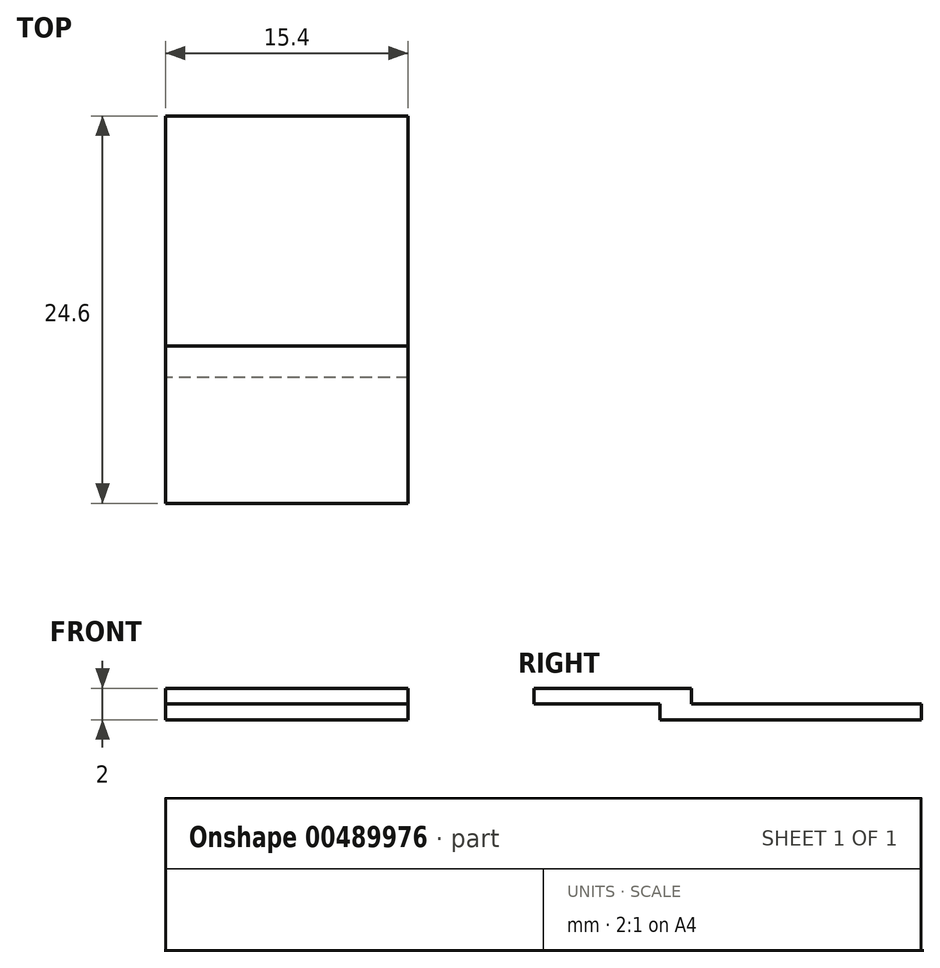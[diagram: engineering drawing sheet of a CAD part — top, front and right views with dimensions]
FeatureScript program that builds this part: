
annotation { "Feature Type Name" : "Feature", "Feature Type Description" : "" }
export const myFeature = defineFeature(function(context is Context, id is Id, definition is map)
    precondition{}
    {
        {
            var Q0;
            Q0=qCreatedBy(makeId("Top.planeOp"),FACE);
            var sketch = newSketch(context, id + "F0", { "sketchPlane" : qUnion([Q0])});
            skLineSegment(sketch, "E0.bottom", {"start": v(7.7, -8.3) * mm, "end": v(-7.7, -8.3) * mm});
            skLineSegment(sketch, "E0.top", {"start": v(7.7, 8.3) * mm, "end": v(-7.7, 8.3) * mm});
            skLineSegment(sketch, "E0.left", {"start": v(7.7, -8.3) * mm, "end": v(7.7, 8.3) * mm});
            skLineSegment(sketch, "E0.right", {"start": v(-7.7, -8.3) * mm, "end": v(-7.7, 8.3) * mm});
            skPoint(sketch, "E0.middle", {"position": v(0, 0) * mm});
            skSolve(sketch);
        }
        {
            var Q0;
            Q0=makeQuery(id+"F0.imprint","IMPRINT",FACE,{"disambiguationData":[TD([[makeQuery(id+"F0.imprint","IMPRINT",EDGE,{"derivedFrom":sQuery(id+"F0.wireOp",EDGE,"E0.bottom")}),-1.0]])]});
            extrude(context, id + "F1", {"entities" : qUnion([Q0]), "depth" : 1 * mm});
        }
        {
            var Q0;
            Q0=makeQuery(id+"F1.opExtrude","CAP_FACE",FACE,{"disambiguationData":[OSD([sQuery(id+"F0.wireOp",EDGE,"E0.bottom"),sQuery(id+"F0.wireOp",EDGE,"E0.top"),sQuery(id+"F0.wireOp",EDGE,"E0.left"),sQuery(id+"F0.wireOp",EDGE,"E0.right")])],"isStart":false});
            cPlane(context, id + "F2", {"entities" : qUnion([Q0]), "cplaneType" : CPlaneType.OFFSET, "offset" : 1 * mm, "width" : 150 * mm, "height" : 150 * mm});
        }
        {
            var Q0;
            Q0=qCreatedBy(id+"F2.planeOp",FACE);
            var sketch = newSketch(context, id + "F3", { "sketchPlane" : qUnion([Q0])});
            skLineSegment(sketch, "E1.bottom", {"start": v(-7.7, -6.3) * mm, "end": v(7.7, -6.3) * mm});
            skLineSegment(sketch, "E1.top", {"start": v(-7.7, -16.3) * mm, "end": v(7.7, -16.3) * mm});
            skLineSegment(sketch, "E1.left", {"start": v(-7.7, -6.3) * mm, "end": v(-7.7, -16.3) * mm});
            skLineSegment(sketch, "E1.right", {"start": v(7.7, -6.3) * mm, "end": v(7.7, -16.3) * mm});
            skSolve(sketch);
        }
        {
            var Q0;
            Q0=makeQuery(id+"F3.imprint","IMPRINT",FACE,{"disambiguationData":[TD([[makeQuery(id+"F3.imprint","IMPRINT",EDGE,{"derivedFrom":sQuery(id+"F3.wireOp",EDGE,"E1.bottom")}),-1.0]])]});
            var Q1;
            Q1=makeQuery(id+"F1.opExtrude","CAP_FACE",FACE,{"disambiguationData":[OSD([sQuery(id+"F0.wireOp",EDGE,"E0.bottom"),sQuery(id+"F0.wireOp",EDGE,"E0.top"),sQuery(id+"F0.wireOp",EDGE,"E0.left"),sQuery(id+"F0.wireOp",EDGE,"E0.right")])],"isStart":false});
            extrude(context, id + "F4", {"entities" : qUnion([Q0]), "operationType" : NewBodyOperationType.ADD, "endBound" : BoundingType.UP_TO_SURFACE, "oppositeDirection" : true, "endBoundEntityFace" : qUnion([Q1]), "depth" : 25 * mm});
        }
    });
